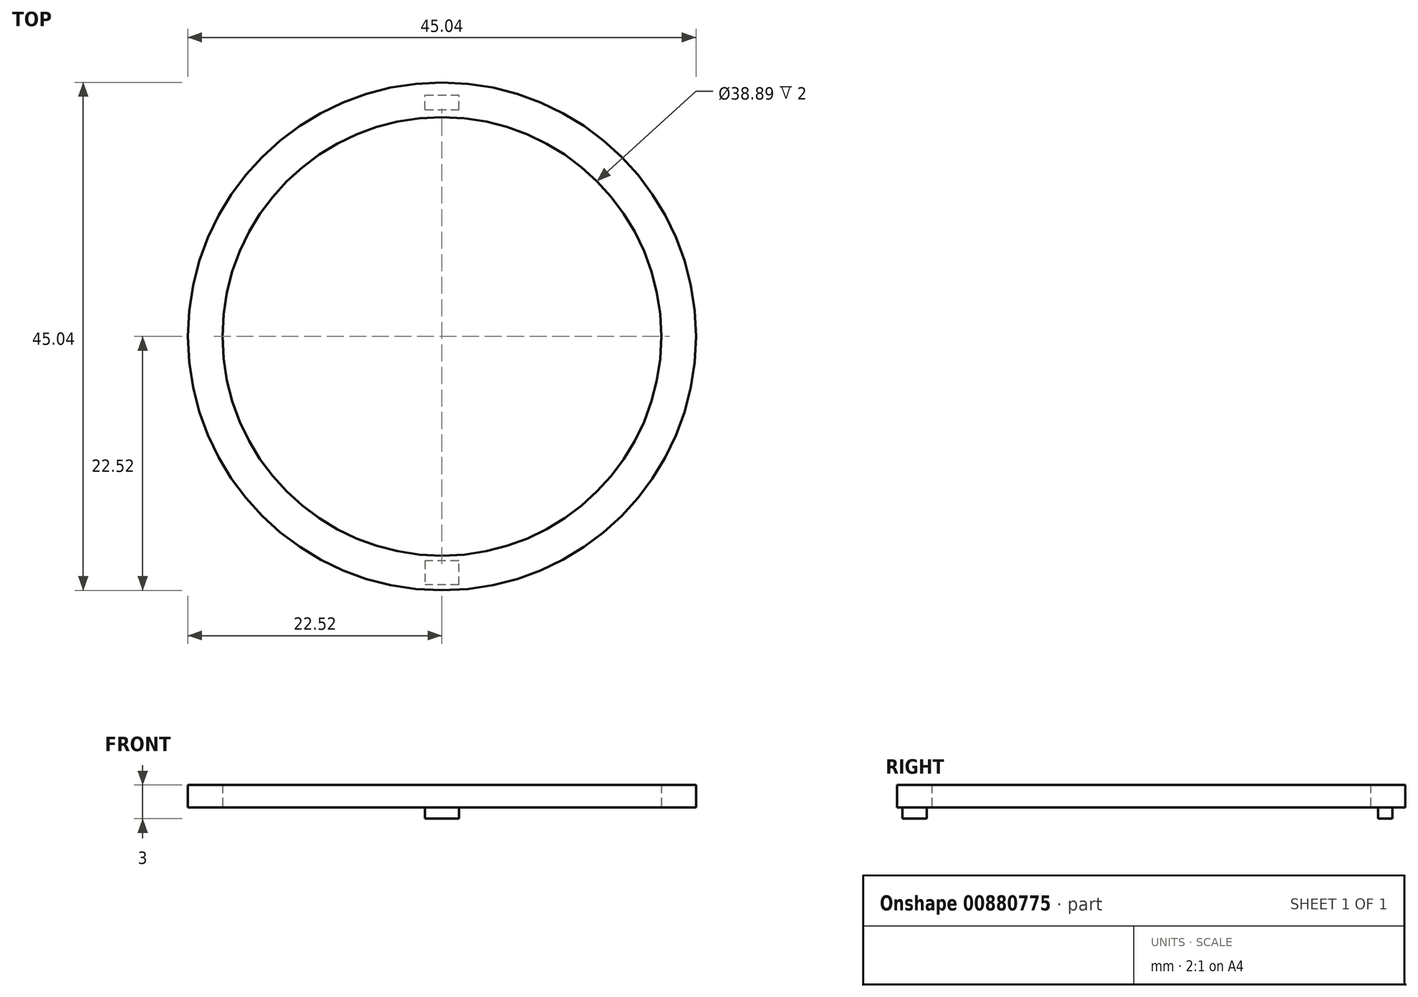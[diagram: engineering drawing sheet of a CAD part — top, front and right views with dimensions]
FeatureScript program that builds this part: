
annotation { "Feature Type Name" : "Feature", "Feature Type Description" : "" }
export const myFeature = defineFeature(function(context is Context, id is Id, definition is map)
    precondition{}
    {
        {
            var Q0;
            Q0=qCreatedBy(makeId("Top.planeOp"),FACE);
            var sketch = newSketch(context, id + "F0", { "sketchPlane" : qUnion([Q0])});
            skCircle(sketch, "E0", {"center": v(0, 0) * mm, "radius": 19.44 * mm});
            skCircle(sketch, "E1", {"center": v(0, 0) * mm, "radius": 22.52 * mm});
            skLineSegment(sketch, "E2.left", {"start": v(-2.92, -19.22) * mm, "end": v(-2.92, -22.33) * mm});
            skLineSegment(sketch, "E3", {"start": v(2.92, 19.22) * mm, "end": v(2.92, 22.33) * mm});
            skLineSegment(sketch, "E4", {"start": v(-2.92, 22.33) * mm, "end": v(-2.92, 19.22) * mm});
            skPoint(sketch, "E5.orphan", {"position": v(-0.07, -19.44) * mm});
            skPoint(sketch, "E6.start.orphan", {"position": v(0, 19.44) * mm});
            skLineSegment(sketch, "E7", {"start": v(-19.22, -2.92) * mm, "end": v(-22.33, -2.92) * mm});
            skLineSegment(sketch, "E8", {"start": v(-22.33, 2.92) * mm, "end": v(-19.22, 2.92) * mm});
            skLineSegment(sketch, "E9", {"start": v(19.22, -2.92) * mm, "end": v(22.33, -2.92) * mm});
            skLineSegment(sketch, "E10", {"start": v(22.33, 2.92) * mm, "end": v(19.22, 2.92) * mm});
            skPoint(sketch, "E11.start.orphan", {"position": v(19.44, 0) * mm});
            skLineSegment(sketch, "E12", {"start": v(2.92, -19.22) * mm, "end": v(2.92, -22.33) * mm});
            skSolve(sketch);
        }
        {
            var Q0;
            {var subQ0=sQuery(id+"F0.wireOp",EDGE,"E3");Q0=makeQuery(id+"F0.imprint","IMPRINT",FACE,{"disambiguationData":[TD([[makeQuery(id+"F0.imprint","IMPRINT",EDGE,{"derivedFrom":subQ0}),1.0]])]});}
            var Q1;
            {var subQ0=sQuery(id+"F0.wireOp",EDGE,"E7");Q1=makeQuery(id+"F0.imprint","IMPRINT",FACE,{"disambiguationData":[TD([[makeQuery(id+"F0.imprint","IMPRINT",EDGE,{"derivedFrom":subQ0}),-1.0]])]});}
            var Q2;
            {var subQ0=sQuery(id+"F0.wireOp",EDGE,"E2.left");Q2=makeQuery(id+"F0.imprint","IMPRINT",FACE,{"disambiguationData":[TD([[makeQuery(id+"F0.imprint","IMPRINT",EDGE,{"derivedFrom":subQ0}),1.0]])]});}
            var Q3;
            {var subQ0=sQuery(id+"F0.wireOp",EDGE,"E9");Q3=makeQuery(id+"F0.imprint","IMPRINT",FACE,{"disambiguationData":[TD([[makeQuery(id+"F0.imprint","IMPRINT",EDGE,{"derivedFrom":subQ0}),1.0]])]});}
            var Q4;
            {var subQ0=sQuery(id+"F0.wireOp",EDGE,"E2.left");Q4=makeQuery(id+"F0.imprint","IMPRINT",FACE,{"disambiguationData":[TD([[makeQuery(id+"F0.imprint","IMPRINT",EDGE,{"derivedFrom":subQ0}),-1.0]])]});}
            var Q5;
            {var subQ0=sQuery(id+"F0.wireOp",EDGE,"E4");Q5=makeQuery(id+"F0.imprint","IMPRINT",FACE,{"disambiguationData":[TD([[makeQuery(id+"F0.imprint","IMPRINT",EDGE,{"derivedFrom":subQ0}),-1.0]])]});}
            var Q6;
            {var subQ0=sQuery(id+"F0.wireOp",EDGE,"E3");Q6=makeQuery(id+"F0.imprint","IMPRINT",FACE,{"disambiguationData":[TD([[makeQuery(id+"F0.imprint","IMPRINT",EDGE,{"derivedFrom":subQ0}),-1.0]])]});}
            var Q7;
            {var subQ0=sQuery(id+"F0.wireOp",EDGE,"E9");Q7=makeQuery(id+"F0.imprint","IMPRINT",FACE,{"disambiguationData":[TD([[makeQuery(id+"F0.imprint","IMPRINT",EDGE,{"derivedFrom":subQ0}),-1.0]])]});}
            extrude(context, id + "F1", {"entities" : qUnion([Q0, Q1, Q2, Q3, Q4, Q5, Q6, Q7]), "depth" : 2 * mm, "offsetDistance" : 25.4 * mm});
        }
        {
            var Q0;
            {var subQ0=sQuery(id+"F0.wireOp",EDGE,"E2.left");Q0=makeQuery(id+"F0.imprint","IMPRINT",FACE,{"disambiguationData":[TD([[makeQuery(id+"F0.imprint","IMPRINT",EDGE,{"derivedFrom":subQ0}),1.0]])]});}
            var sketch = newSketch(context, id + "F2", { "sketchPlane" : qUnion([Q0])});
            skLineSegment(sketch, "E13.bottom", {"start": v(1.5, -22.04) * mm, "end": v(-1.5, -22.04) * mm});
            skPoint(sketch, "E13.middle", {"position": v(0, -20.14) * mm});
            skPoint(sketch, "E13.top.end.orphan", {"position": v(-1.5, -18.24) * mm});
            skPoint(sketch, "E13.top.start.orphan", {"position": v(1.5, -18.24) * mm});
            skLineSegment(sketch, "E14", {"start": v(1.5, -22.04) * mm, "end": v(1.5, -19.88) * mm});
            skLineSegment(sketch, "E15", {"start": v(1.5, -19.88) * mm, "end": v(-1.5, -19.88) * mm});
            skLineSegment(sketch, "E16", {"start": v(-1.5, -19.88) * mm, "end": v(-1.5, -22.04) * mm});
            skLineSegment(sketch, "E17", {"start": v(-13.3, 0) * mm, "end": v(12.35, 0) * mm});
            skLineSegment(sketch, "E18.bottom", {"start": v(-1.5, 20.11) * mm, "end": v(1.5, 20.11) * mm});
            skLineSegment(sketch, "E18.top", {"start": v(-1.5, 21.4) * mm, "end": v(1.5, 21.4) * mm});
            skLineSegment(sketch, "E18.left", {"start": v(-1.5, 20.11) * mm, "end": v(-1.5, 21.4) * mm});
            skLineSegment(sketch, "E18.right", {"start": v(1.5, 20.11) * mm, "end": v(1.5, 21.4) * mm});
            skPoint(sketch, "E18.middle", {"position": v(0, 20.75) * mm});
            skSolve(sketch);
        }
        {
            var Q0;
            Q0=makeQuery(id+"F2.imprint","IMPRINT",FACE,{"disambiguationData":[TD([[makeQuery(id+"F2.imprint","IMPRINT",EDGE,{"derivedFrom":sQuery(id+"F2.wireOp",EDGE,"E18.bottom")}),1.0]])]});
            var Q1;
            Q1=makeQuery(id+"F2.imprint","IMPRINT",FACE,{"disambiguationData":[TD([[makeQuery(id+"F2.imprint","IMPRINT",EDGE,{"derivedFrom":sQuery(id+"F2.wireOp",EDGE,"E13.bottom")}),-1.0]])]});
            extrude(context, id + "F3", {"entities" : qUnion([Q0, Q1]), "operationType" : NewBodyOperationType.ADD, "oppositeDirection" : true, "depth" : 1 * mm, "offsetDistance" : 25.4 * mm});
        }
    });
